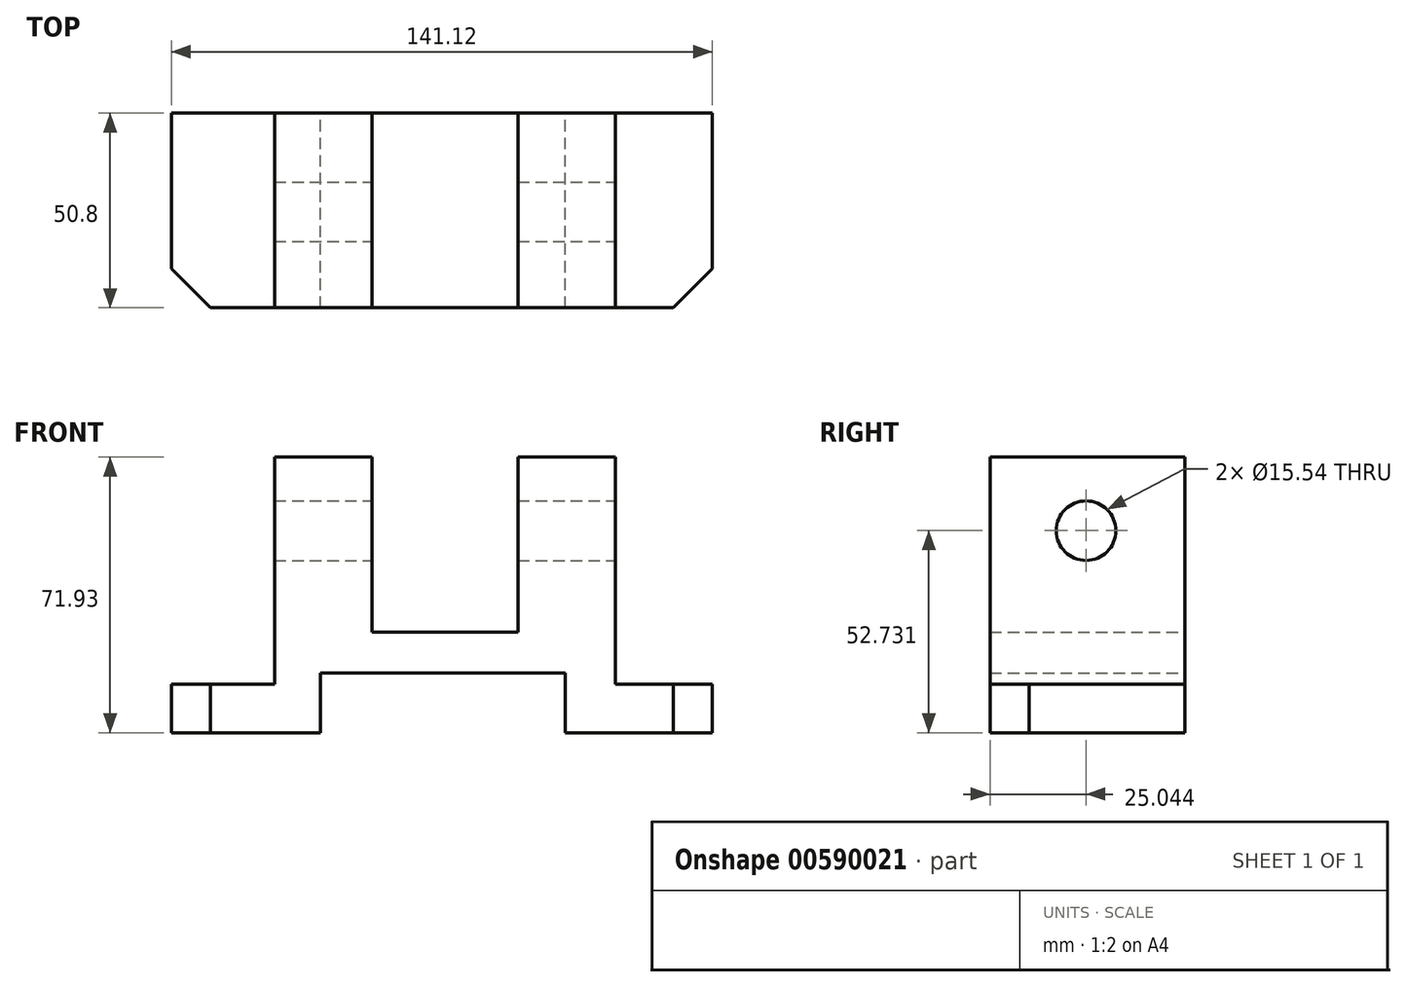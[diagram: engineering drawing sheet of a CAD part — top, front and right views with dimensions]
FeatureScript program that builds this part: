
annotation { "Feature Type Name" : "Feature", "Feature Type Description" : "" }
export const myFeature = defineFeature(function(context is Context, id is Id, definition is map)
    precondition{}
    {
        {
            var Q0;
            Q0=qCreatedBy(makeId("Front.planeOp"),FACE);
            var sketch = newSketch(context, id + "F0", { "sketchPlane" : qUnion([Q0])});
            skLineSegment(sketch, "E0", {"start": v(-84.78, -39.32) * mm, "end": v(-84.78, -26.62) * mm});
            skLineSegment(sketch, "E1", {"start": v(-84.78, -26.62) * mm, "end": v(-70.56, -26.62) * mm});
            skLineSegment(sketch, "E2", {"start": v(-70.56, -26.62) * mm, "end": v(-70.56, 32.61) * mm});
            skLineSegment(sketch, "E3", {"start": v(-70.56, 32.61) * mm, "end": v(-45.16, 32.61) * mm});
            skLineSegment(sketch, "E4", {"start": v(-45.16, -13.1) * mm, "end": v(-45.16, 32.61) * mm});
            skLineSegment(sketch, "E5", {"start": v(-45.16, -13.1) * mm, "end": v(-7.06, -13.1) * mm});
            skLineSegment(sketch, "E6", {"start": v(-7.06, 32.61) * mm, "end": v(-7.06, -13.1) * mm});
            skLineSegment(sketch, "E7", {"start": v(-7.06, 32.61) * mm, "end": v(18.34, 32.61) * mm});
            skLineSegment(sketch, "E8", {"start": v(18.34, 32.61) * mm, "end": v(18.34, -26.62) * mm});
            skLineSegment(sketch, "E9", {"start": v(18.34, -26.62) * mm, "end": v(30.94, -26.62) * mm});
            skLineSegment(sketch, "E10", {"start": v(30.94, -26.62) * mm, "end": v(30.94, -39.32) * mm});
            skLineSegment(sketch, "E11", {"start": v(30.94, -39.32) * mm, "end": v(5.33, -39.32) * mm});
            skLineSegment(sketch, "E12", {"start": v(5.33, -39.32) * mm, "end": v(5.33, -23.77) * mm});
            skLineSegment(sketch, "E13", {"start": v(5.33, -23.77) * mm, "end": v(-58.57, -23.77) * mm});
            skLineSegment(sketch, "E14", {"start": v(-58.57, -23.77) * mm, "end": v(-58.57, -39.32) * mm});
            skLineSegment(sketch, "E15", {"start": v(-84.78, -39.32) * mm, "end": v(-58.57, -39.32) * mm});
            skLineSegment(sketch, "E16", {"start": v(30.94, -26.62) * mm, "end": v(43.64, -26.62) * mm});
            skLineSegment(sketch, "E17", {"start": v(43.64, -26.62) * mm, "end": v(43.64, -39.32) * mm});
            skLineSegment(sketch, "E18", {"start": v(43.64, -39.32) * mm, "end": v(30.94, -39.32) * mm});
            skLineSegment(sketch, "E19", {"start": v(-84.78, -39.32) * mm, "end": v(-97.48, -39.32) * mm});
            skLineSegment(sketch, "E20", {"start": v(-84.78, -26.62) * mm, "end": v(-97.48, -26.62) * mm});
            skLineSegment(sketch, "E21", {"start": v(-97.48, -26.62) * mm, "end": v(-97.48, -39.32) * mm});
            skSolve(sketch);
        }
        {
            var Q0;
            Q0=makeQuery(id+"F0.imprint","IMPRINT",FACE,{"disambiguationData":[TD([[makeQuery(id+"F0.imprint","IMPRINT",EDGE,{"derivedFrom":sQuery(id+"F0.wireOp",EDGE,"E10")}),1.0]])]});
            var Q1;
            Q1=makeQuery(id+"F0.imprint","IMPRINT",FACE,{"disambiguationData":[TD([[makeQuery(id+"F0.imprint","IMPRINT",EDGE,{"derivedFrom":sQuery(id+"F0.wireOp",EDGE,"E0")}),1.0]])]});
            var Q2;
            Q2=makeQuery(id+"F0.imprint","IMPRINT",FACE,{"disambiguationData":[TD([[makeQuery(id+"F0.imprint","IMPRINT",EDGE,{"derivedFrom":sQuery(id+"F0.wireOp",EDGE,"E0")}),-1.0]])]});
            extrude(context, id + "F1", {"entities" : qUnion([Q0, Q1, Q2]), "depth" : 50.8 * mm, "offsetDistance" : 25.4 * mm});
        }
        {
            var Q0;
            Q0=makeQuery(id+"F1.opExtrude","CAP_EDGE",EDGE,{"disambiguationData":[OSD([sQuery(id+"F0.wireOp",EDGE,"E17")])],"isStart":false});
            chamfer(context, id + "F2", {"entities" : qUnion([Q0]), "width" : 10.16 * mm, "tangentPropagation" : true});
        }
        {
            var Q0;
            Q0=makeQuery(id+"F1.opExtrude","CAP_EDGE",EDGE,{"disambiguationData":[OSD([sQuery(id+"F0.wireOp",EDGE,"E21")])],"isStart":false});
            chamfer(context, id + "F3", {"entities" : qUnion([Q0]), "width" : 10.16 * mm, "tangentPropagation" : true});
        }
        {
            var Q0;
            Q0=makeQuery(id+"F1.opExtrude","SWEPT_FACE",FACE,{"disambiguationData":[OSD([sQuery(id+"F0.wireOp",EDGE,"E8")])]});
            var sketch = newSketch(context, id + "F4", { "sketchPlane" : qUnion([Q0])});
            skCircle(sketch, "E22", {"center": v(-25.76, 13.41) * mm, "radius": 7.77 * mm});
            skSolve(sketch);
        }
        {
            var Q0;
            Q0=makeQuery(id+"F4.imprint","IMPRINT",FACE,{"disambiguationData":[TD([[makeQuery(id+"F4.imprint","IMPRINT",EDGE,{"derivedFrom":sQuery(id+"F4.wireOp",EDGE,"E22")}),1.0]])]});
            extrude(context, id + "F5", {"entities" : qUnion([Q0]), "operationType" : NewBodyOperationType.REMOVE, "oppositeDirection" : true, "depth" : 99.57 * mm, "offsetDistance" : 25.4 * mm});
        }
    });
